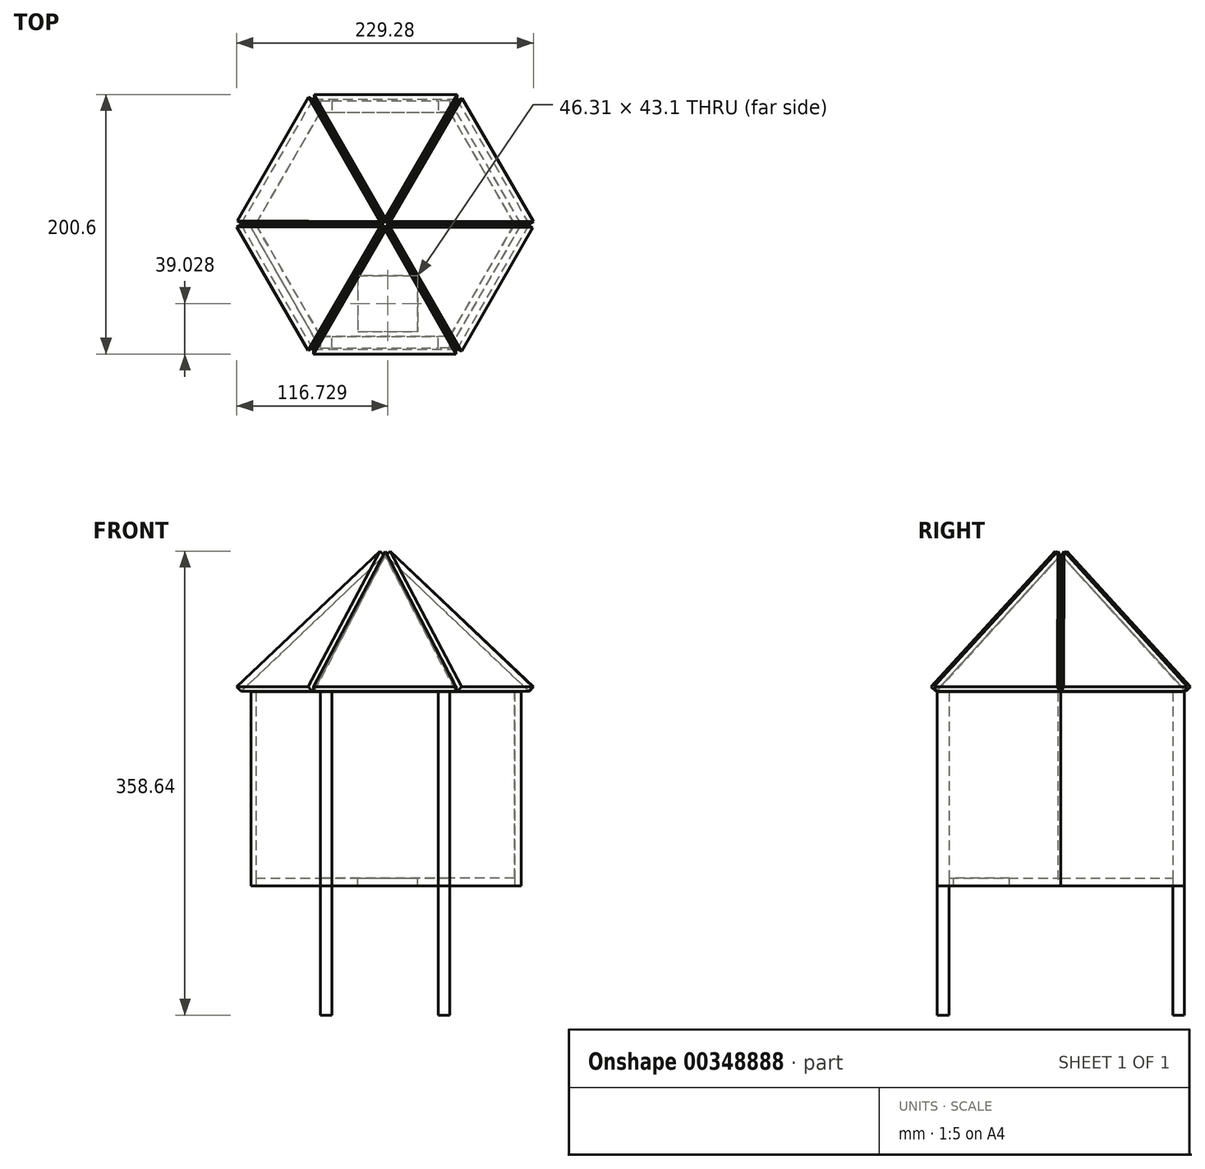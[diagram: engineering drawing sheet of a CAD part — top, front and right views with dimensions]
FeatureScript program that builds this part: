
annotation { "Feature Type Name" : "Feature", "Feature Type Description" : "" }
export const myFeature = defineFeature(function(context is Context, id is Id, definition is map)
    precondition{}
    {
        {
            var Q0;
            Q0=qCreatedBy(makeId("Top.planeOp"),FACE);
            var sketch = newSketch(context, id + "F0", { "sketchPlane" : qUnion([Q0])});
            skCircle(sketch, "E0.cCircle", {"center": v(0, 0) * mm, "radius": 86.6 * mm, "construction": true});
            skLineSegment(sketch, "E0.0", {"start": v(50, 86.6) * mm, "end": v(100, 0) * mm});
            skLineSegment(sketch, "E0.1", {"start": v(100, 0) * mm, "end": v(50, -86.6) * mm});
            skLineSegment(sketch, "E0.2", {"start": v(50, -86.6) * mm, "end": v(-50, -86.6) * mm});
            skLineSegment(sketch, "E0.3", {"start": v(-50, -86.6) * mm, "end": v(-100, 0) * mm});
            skLineSegment(sketch, "E0.4", {"start": v(-100, 0) * mm, "end": v(-50, 86.6) * mm});
            skLineSegment(sketch, "E0.5", {"start": v(-50, 86.6) * mm, "end": v(50, 86.6) * mm});
            skPoint(sketch, "E0.0.midPoint", {"position": v(75, 43.3) * mm});
            skLineSegment(sketch, "E1", {"start": v(-146.24, 86.6) * mm, "end": v(86.54, 86.6) * mm, "construction": true});
            skLineSegment(sketch, "E2", {"start": v(-88.7, 0) * mm, "end": v(0, 0) * mm, "construction": true});
            skPoint(sketch, "E2.endSnap0", {"position": v(0, -86.6) * mm});
            skLineSegment(sketch, "E3", {"start": v(0, 102.14) * mm, "end": v(0, -90.63) * mm, "construction": true});
            skPoint(sketch, "E3.startSnap0", {"position": v(0, 86.6) * mm});
            skSolve(sketch);
        }
        {
            var Q0;
            Q0=qSketchRegion(id+"F0",true);
            extrude(context, id + "F1", {"entities" : qUnion([Q0]), "depth" : 6 * mm});
        }
        {
            var Q0;
            Q0=qCreatedBy(makeId("Top.planeOp"),FACE);
            var sketch = newSketch(context, id + "F2", { "sketchPlane" : qUnion([Q0])});
            skLineSegment(sketch, "E4.bottom", {"start": v(-50, 95.6) * mm, "end": v(-41, 95.6) * mm});
            skLineSegment(sketch, "E4.top", {"start": v(-50, 86.6) * mm, "end": v(-41, 86.6) * mm});
            skLineSegment(sketch, "E4.left", {"start": v(-50, 95.6) * mm, "end": v(-50, 86.6) * mm});
            skLineSegment(sketch, "E4.right", {"start": v(-41, 95.6) * mm, "end": v(-41, 86.6) * mm});
            skLineSegment(sketch, "E5", {"start": v(-41, -733.2) * mm, "end": v(-45.5, -538.98) * mm, "construction": true});
            skPoint(sketch, "E5.startSnap0", {"position": v(-41, 91.1) * mm});
            skPoint(sketch, "E5.endSnap0", {"position": v(-45.5, 95.6) * mm});
            skLineSegment(sketch, "E6", {"start": v(50, 110.57) * mm, "end": v(50, -106.48) * mm, "construction": true});
            skLineSegment(sketch, "E7", {"start": v(0, 118.71) * mm, "end": v(0, -106.48) * mm, "construction": true});
            skLineSegment(sketch, "E8", {"start": v(-50, 122.55) * mm, "end": v(-50, -106.48) * mm, "construction": true});
            skPoint(sketch, "E9.MirrorP", {"position": v(45.5, 95.6) * mm});
            skPoint(sketch, "E10.MirrorP", {"position": v(41, 91.1) * mm});
            skLineSegment(sketch, "E11.MirrorCS", {"start": v(50, 95.6) * mm, "end": v(41, 95.6) * mm});
            skLineSegment(sketch, "E12.MirrorCS", {"start": v(50, 86.6) * mm, "end": v(41, 86.6) * mm});
            skLineSegment(sketch, "E13.MirrorCS", {"start": v(50, 95.6) * mm, "end": v(50, 86.6) * mm});
            skLineSegment(sketch, "E14.MirrorCS", {"start": v(41, 95.6) * mm, "end": v(41, 86.6) * mm});
            skLineSegment(sketch, "E15", {"start": v(-110.42, 0) * mm, "end": v(140.1, 0) * mm, "construction": true});
            skLineSegment(sketch, "E16.MirrorCS", {"start": v(-41, -95.6) * mm, "end": v(-41, -86.6) * mm});
            skLineSegment(sketch, "E17.MirrorCS", {"start": v(50, -95.6) * mm, "end": v(41, -95.6) * mm});
            skLineSegment(sketch, "E18.MirrorCS", {"start": v(50, -86.6) * mm, "end": v(41, -86.6) * mm});
            skLineSegment(sketch, "E19.MirrorCS", {"start": v(50, -95.6) * mm, "end": v(50, -86.6) * mm});
            skLineSegment(sketch, "E20.MirrorCS", {"start": v(41, -95.6) * mm, "end": v(41, -86.6) * mm});
            skLineSegment(sketch, "E21.MirrorCS", {"start": v(-50, -86.6) * mm, "end": v(-41, -86.6) * mm});
            skLineSegment(sketch, "E22.MirrorCS", {"start": v(-50, -95.6) * mm, "end": v(-50, -86.6) * mm});
            skLineSegment(sketch, "E23.MirrorCS", {"start": v(-50, -95.6) * mm, "end": v(-41, -95.6) * mm});
            skPoint(sketch, "E24.MirrorP", {"position": v(-45.5, -95.6) * mm});
            skPoint(sketch, "E25.MirrorP", {"position": v(45.5, -95.6) * mm});
            skPoint(sketch, "E26.MirrorP", {"position": v(41, -91.1) * mm});
            skPoint(sketch, "E27.MirrorP", {"position": v(-41, -91.1) * mm});
            skSolve(sketch);
        }
        {
            var Q0;
            Q0=qSketchRegion(id+"F2",true);
            extrude(context, id + "F3", {"entities" : qUnion([Q0]), "depth" : 150 * mm});
        }
        {
            var Q0;
            Q0=qCreatedBy(makeId("Top.planeOp"),FACE);
            cPlane(context, id + "F4", {"entities" : qUnion([Q0]), "cplaneType" : CPlaneType.OFFSET, "offset" : 150 * mm, "width" : 150 * mm, "height" : 150 * mm});
        }
        {
            var Q0;
            Q0=qCreatedBy(id+"F4.planeOp",FACE);
            var sketch = newSketch(context, id + "F5", { "sketchPlane" : qUnion([Q0])});
            skLineSegment(sketch, "E28.bottom", {"start": v(-41, 95.6) * mm, "end": v(41, 95.6) * mm});
            skLineSegment(sketch, "E28.top", {"start": v(-41, 86.6) * mm, "end": v(41, 86.6) * mm});
            skLineSegment(sketch, "E28.left", {"start": v(-41, 95.6) * mm, "end": v(-41, 86.6) * mm});
            skLineSegment(sketch, "E28.right", {"start": v(41, 95.6) * mm, "end": v(41, 86.6) * mm});
            skSolve(sketch);
        }
        {
            var Q0;
            Q0=qSketchRegion(id+"F5",true);
            extrude(context, id + "F6", {"entities" : qUnion([Q0]), "oppositeDirection" : true, "depth" : 150 * mm});
        }
        {
            var Q0;
            Q0=makeQuery(id+"F6.opExtrude","SWEPT_BODY",BODY,{"disambiguationData":[OSD([sQuery(id+"F5.wireOp",EDGE,"E28.bottom"),sQuery(id+"F5.wireOp",EDGE,"E28.top"),sQuery(id+"F5.wireOp",EDGE,"E28.left"),sQuery(id+"F5.wireOp",EDGE,"E28.right")])]});
            var Q1;
            Q1=qCreatedBy(makeId("Front.planeOp"),FACE);
            mirror(context, id + "F7", {"entities" : qUnion([Q0]), "mirrorPlane" : qUnion([Q1])});
        }
        {
            var Q0;
            Q0=qSketchRegion(id+"F2",true);
            var Q1;
            Q1=qConstructionFilter(qBodyType(qCreatedBy(id+"F2",EDGE),BodyType.WIRE),ConstructionObject.NO);
            extrude(context, id + "F8", {"entities" : qUnion([Q0]), "surfaceEntities" : qUnion([Q1]), "oppositeDirection" : true, "depth" : 100 * mm});
        }
        {
            var Q0;
            Q0=qCreatedBy(id+"F4.planeOp",FACE);
            var sketch = newSketch(context, id + "F9", { "sketchPlane" : qUnion([Q0])});
            skLineSegment(sketch, "E29", {"start": v(50, 86.6) * mm, "end": v(100, 0) * mm});
            skLineSegment(sketch, "E30", {"start": v(100, 0) * mm, "end": v(105.2, 0) * mm});
            skLineSegment(sketch, "E31", {"start": v(105.2, 0) * mm, "end": v(50, 95.6) * mm});
            skLineSegment(sketch, "E32", {"start": v(50, 95.6) * mm, "end": v(50, 86.6) * mm});
            skLineSegment(sketch, "E33", {"start": v(0, 117.97) * mm, "end": v(0, 29.71) * mm, "construction": true});
            skSolve(sketch);
        }
        {
            var Q0;
            Q0=qSketchRegion(id+"F9",true);
            extrude(context, id + "F10", {"entities" : qUnion([Q0]), "operationType" : NewBodyOperationType.ADD, "oppositeDirection" : true, "depth" : 150 * mm});
        }
        {
            var Q0;
            Q0=qCreatedBy(makeId("Front.planeOp"),FACE);
            var sketch = newSketch(context, id + "F11", { "sketchPlane" : qUnion([Q0])});
            skLineSegment(sketch, "E34", {"start": v(0, 297.87) * mm, "end": v(0, -100.74) * mm, "construction": true});
            skCircle(sketch, "E35", {"center": v(0, 226.82) * mm, "radius": 12.33 * mm, "construction": true});
            skSolve(sketch);
        }
        {
            var Q0;
            Q0=makeQuery(id+"F1.opExtrude","CAP_FACE",FACE,{"disambiguationData":[OSD([sQuery(id+"F0.wireOp",EDGE,"E0.0"),sQuery(id+"F0.wireOp",EDGE,"E0.1"),sQuery(id+"F0.wireOp",EDGE,"E0.2"),sQuery(id+"F0.wireOp",EDGE,"E0.3"),sQuery(id+"F0.wireOp",EDGE,"E0.4"),sQuery(id+"F0.wireOp",EDGE,"E0.5")])],"isStart":false});
            var sketch = newSketch(context, id + "F12", { "sketchPlane" : qUnion([Q0])});
            skLineSegment(sketch, "E36.bottom", {"start": v(-21.07, -39.72) * mm, "end": v(25.24, -39.72) * mm});
            skLineSegment(sketch, "E36.top", {"start": v(-21.07, -82.82) * mm, "end": v(25.24, -82.82) * mm});
            skLineSegment(sketch, "E36.left", {"start": v(-21.07, -39.72) * mm, "end": v(-21.07, -82.82) * mm});
            skLineSegment(sketch, "E36.right", {"start": v(25.24, -39.72) * mm, "end": v(25.24, -82.82) * mm});
            skSolve(sketch);
        }
        {
            var Q0;
            Q0=makeQuery(id+"F12.imprint","IMPRINT",FACE,{"disambiguationData":[TD([[makeQuery(id+"F12.imprint","IMPRINT",EDGE,{"derivedFrom":sQuery(id+"F12.wireOp",EDGE,"E36.bottom")}),-1.0]])]});
            extrude(context, id + "F13", {"entities" : qUnion([Q0]), "operationType" : NewBodyOperationType.REMOVE, "endBound" : BoundingType.UP_TO_NEXT, "oppositeDirection" : true, "depth" : 25 * mm});
        }
        {
            var Q0;
            Q0=qCreatedBy(makeId("Top.planeOp"),FACE);
            var sketch = newSketch(context, id + "F14", { "sketchPlane" : qUnion([Q0])});
            skLineSegment(sketch, "E37", {"start": v(100, 0) * mm, "end": v(105.2, 0) * mm});
            skLineSegment(sketch, "E38", {"start": v(105.2, 0) * mm, "end": v(50, -95.6) * mm});
            skLineSegment(sketch, "E39", {"start": v(50, -95.6) * mm, "end": v(50, -86.6) * mm});
            skLineSegment(sketch, "E40", {"start": v(50, -86.6) * mm, "end": v(100, 0) * mm});
            skSolve(sketch);
        }
        {
            var Q0;
            Q0=qCreatedBy(makeId("Top.planeOp"),FACE);
            var sketch = newSketch(context, id + "F15", { "sketchPlane" : qUnion([Q0])});
            skLineSegment(sketch, "E41", {"start": v(-103.82, -2.2) * mm, "end": v(-100, 0) * mm});
            skLineSegment(sketch, "E42", {"start": v(-100, 0) * mm, "end": v(-50, -86.6) * mm});
            skLineSegment(sketch, "E43", {"start": v(-50, -86.6) * mm, "end": v(-50, -95.6) * mm});
            skLineSegment(sketch, "E44", {"start": v(-50, -95.6) * mm, "end": v(-103.82, -2.2) * mm});
            skSolve(sketch);
        }
        {
            var Q0;
            Q0=qSketchRegion(id+"F14",true);
            extrude(context, id + "F16", {"entities" : qUnion([Q0]), "depth" : 150 * mm});
        }
        {
            var Q0;
            Q0=qSketchRegion(id+"F15",true);
            extrude(context, id + "F17", {"entities" : qUnion([Q0]), "depth" : 150 * mm});
        }
        {
            var Q0;
            Q0=qCreatedBy(id+"F4.planeOp",FACE);
            var sketch = newSketch(context, id + "F18", { "sketchPlane" : qUnion([Q0])});
            skCircle(sketch, "E45.cCircle", {"center": v(0, 0) * mm, "radius": 96.97 * mm, "construction": true});
            skLineSegment(sketch, "E45.0", {"start": v(111.97, 0) * mm, "end": v(55.99, -96.97) * mm});
            skLineSegment(sketch, "E45.1", {"start": v(55.99, -96.97) * mm, "end": v(-55.99, -96.97) * mm});
            skLineSegment(sketch, "E45.2", {"start": v(-55.99, -96.97) * mm, "end": v(-111.97, 0) * mm});
            skLineSegment(sketch, "E45.3", {"start": v(-111.97, 0) * mm, "end": v(-55.99, 96.97) * mm});
            skLineSegment(sketch, "E45.4", {"start": v(-55.99, 96.97) * mm, "end": v(55.99, 96.97) * mm});
            skLineSegment(sketch, "E45.5", {"start": v(55.99, 96.97) * mm, "end": v(111.97, 0) * mm});
            skPoint(sketch, "E45.0.midPoint", {"position": v(83.98, -48.49) * mm});
            skSolve(sketch);
        }
        {
            var Q0;
            Q0=qCreatedBy(makeId("Right.planeOp"),FACE);
            var sketch = newSketch(context, id + "F19", { "sketchPlane" : qUnion([Q0])});
            skLineSegment(sketch, "E46", {"start": v(-96.97, 150) * mm, "end": v(0, 256.22) * mm});
            skSolve(sketch);
        }
        {
            var Q0;
            Q0=sQuery(id+"F19.wireOp",VERTEX,"E46.end");
            var Q1;
            Q1=sQuery(id+"F18.wireOp",VERTEX,"E45.2.start");
            var Q2;
            Q2=sQuery(id+"F18.wireOp",VERTEX,"E45.1.start");
            cPlane(context, id + "F20", {"entities" : qUnion([Q0, Q1, Q2]), "cplaneType" : CPlaneType.THREE_POINT, "offset" : 25 * mm, "width" : 150 * mm, "height" : 150 * mm});
        }
        {
            var Q0;
            Q0=qCreatedBy(id+"F20.planeOp",FACE);
            var sketch = newSketch(context, id + "F21", { "sketchPlane" : qUnion([Q0])});
            skLineSegment(sketch, "E47", {"start": v(0, 187.94) * mm, "end": v(55.56, 45.94) * mm});
            skLineSegment(sketch, "E48", {"start": v(55.56, 45.94) * mm, "end": v(-54.75, 45.94) * mm});
            skLineSegment(sketch, "E49", {"start": v(-54.75, 45.94) * mm, "end": v(0, 187.94) * mm});
            skSolve(sketch);
        }
        {
            var Q0;
            Q0=qSketchRegion(id+"F21",true);
            extrude(context, id + "F22", {"entities" : qUnion([Q0]), "oppositeDirection" : true, "depth" : 5 * mm});
        }
        {
            var Q0;
            Q0=makeQuery(id+"F22.opExtrude","SWEPT_BODY",BODY,{"disambiguationData":[OSD([sQuery(id+"F21.wireOp",EDGE,"E47"),sQuery(id+"F21.wireOp",EDGE,"E48"),sQuery(id+"F21.wireOp",EDGE,"E49")])]});
            var Q1;
            Q1=sQuery(id+"F11.wireOp",EDGE,"E34");
            circularPattern(context, id + "F23", {"entities" : qUnion([Q0]), "axis" : qUnion([Q1]), "angle" : 360 * degree, "instanceCount" : 6, "equalSpace" : true});
        }
    });
